# Revit family: Fu_Table_Sandler_Arc 90
name_source: partatom
category: Furniture
units: mm (PartAtom-declared; Revit-internal decimal feet)

## family parameters
Always vertical = Yes
Cut with Voids When Loaded = No
OmniClass Number = 23.40.20.00
OmniClass Title = General Furniture and Specialties
Room Calculation Point = No
Shared = No
Work Plane-Based = No

## types (1)
- Arc 90
    Default Elevation = 0 mm  [stored 0 ft]
    Depth = 900 mm  [stored 2.95276 ft]
    Description = Round table with steel base and wood top in oak, walnut or lacquered finish. Top size 90 cm/36″ diameter, base spread 50 cm/20″ diameter.
    Height = 720 mm  [stored 2.3622 ft]
    Manufacturer = Sandler
    Model = Arc 90
    URL = https://www.sandlerseating.com
    Width = 900 mm  [stored 2.95276 ft]

note: [stored X ft] marks values corroborated as IEEE doubles in the binary element streams (Revit-internal decimal feet)

## geometry (parser evidence)
native form markers: Sweep x3
no freeform markers — native parametric forms only
